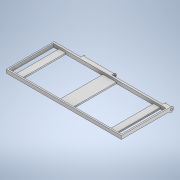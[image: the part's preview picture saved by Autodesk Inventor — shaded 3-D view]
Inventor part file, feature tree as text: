
AUTODESK INVENTOR PART (.ipt)
format: ipt  version: 2021 (Build 250183000, 183)  size: 177,664 bytes
history: native  units: mm
features: extrude x5, sketch x5, projected_geometry x2
ambient origin geometry x8: Origin, YZ Plane, XZ Plane, XY Plane, X Axis, Y Axis, Z Axis, Center Point
bodies: Volumenkörper1 (feature_tree)
feature tree (12):
  extrude  "Extrusion1"  Depth=70.0mm
  extrude  "Extrusion2"  Depth=2.0mm
  extrude  "Extrusion3"  Depth=20.0mm
  extrude  "Extrusion4"  Depth=10.0mm
  extrude  "Extrusion5"  TaperAngle=0.0deg  [1 undecoded]
  sketch  "Skizze1"  dims[d0=170.0mm d1=70.0mm]
  sketch  "Skizze2"  dims[d2=5.0mm d3=0.0mm d4=2.0mm]
  projected_geometry  "Projizierte Kontur1"
  sketch  "Skizze3"  dims[d5=3.0mm d6=0.0mm d7=20.0mm]
  projected_geometry  "Projizierte Kontur2"
  sketch  "Skizze4"  dims[d8=10.0mm d9=10.0mm]
  sketch  "Skizze5"  dims[d10=10.0mm d11=0.0mm d12=0.0mm d13=7.0mm d14=3.5mm d17=3.0mm d18=0.0mm d25=0.0mm d26=0.0mm d27=4.0mm d28=0.5mm d29=9.5mm d30=9.5mm d31=30.0mm d32=30.0mm]
note: 1 required parameter value undecoded (feature->parameter linkage not recoverable at this tier; creation-order binding heuristic only, values carry confidence <= 0.55)
